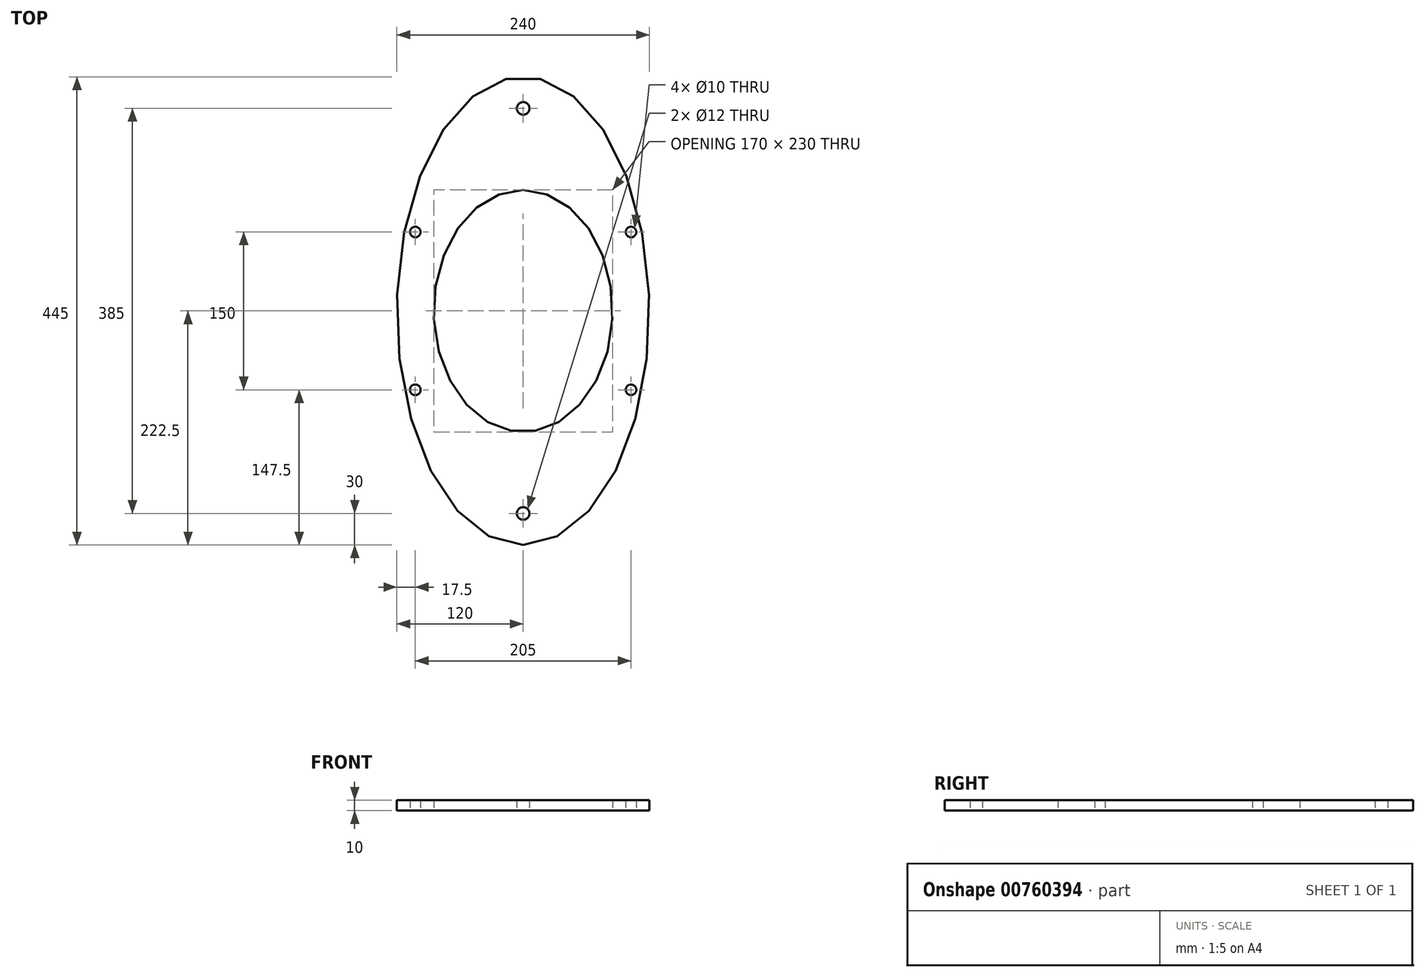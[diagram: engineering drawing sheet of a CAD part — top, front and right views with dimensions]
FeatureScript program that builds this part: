
annotation { "Feature Type Name" : "Feature", "Feature Type Description" : "" }
export const myFeature = defineFeature(function(context is Context, id is Id, definition is map)
    precondition{}
    {
        {
            var Q0;
            Q0=qCreatedBy(makeId("Top.planeOp"),FACE);
            var sketch = newSketch(context, id + "F0", { "sketchPlane" : qUnion([Q0])});
            skPoint(sketch, "E0", {"position": v(150.32, -165.76) * mm});
            skPoint(sketch, "E1", {"position": v(107.37, -221.56) * mm});
            skPoint(sketch, "E2", {"position": v(69.02, -211.72) * mm});
            skPoint(sketch, "E3", {"position": v(0, -246.18) * mm});
            skPoint(sketch, "E4", {"position": v(138.05, -177.25) * mm});
            skPoint(sketch, "E5", {"position": v(146.48, 0) * mm});
            skPoint(sketch, "E6", {"position": v(132.68, -82.88) * mm});
            skLineSegment(sketch, "E7", {"start": v(0, 292) * mm, "end": v(0, -246.18) * mm, "construction": true});
            skPoint(sketch, "E8.MirrorP", {"position": v(-146.48, 0) * mm});
            skPoint(sketch, "E9.MirrorP", {"position": v(-132.68, -82.88) * mm});
            skPoint(sketch, "E10.MirrorP", {"position": v(-150.32, -165.76) * mm});
            skPoint(sketch, "E11.MirrorP", {"position": v(-138.05, -177.25) * mm});
            skPoint(sketch, "E12.MirrorP", {"position": v(-107.37, -221.56) * mm});
            skPoint(sketch, "E13.MirrorP", {"position": v(-69.02, -211.72) * mm});
            skPoint(sketch, "E14", {"position": v(0, 0) * mm});
            skPoint(sketch, "E15", {"position": v(-146.25, -161.4) * mm});
            skPoint(sketch, "E16", {"position": v(-136.87, -189.28) * mm});
            skPoint(sketch, "E17", {"position": v(-146.26, -172.33) * mm});
            skPoint(sketch, "E18", {"position": v(-131.04, -210.06) * mm});
            skPoint(sketch, "E19", {"position": v(-94.82, -218.38) * mm});
            skPoint(sketch, "E20", {"position": v(-60.59, -222.84) * mm});
            skPoint(sketch, "E21", {"position": v(-67.25, -214.49) * mm});
            skPoint(sketch, "E22", {"position": v(-72.48, -210.2) * mm});
            skPoint(sketch, "E23", {"position": v(-119.37, -219.05) * mm});
            skPoint(sketch, "E24", {"position": v(-149.89, -167.68) * mm});
            skPoint(sketch, "E25.MirrorP", {"position": v(60.59, -222.84) * mm});
            skPoint(sketch, "E26.MirrorP", {"position": v(67.25, -214.49) * mm});
            skPoint(sketch, "E27.MirrorP", {"position": v(72.48, -210.2) * mm});
            skPoint(sketch, "E28.MirrorP", {"position": v(94.82, -218.38) * mm});
            skPoint(sketch, "E29.MirrorP", {"position": v(119.37, -219.05) * mm});
            skPoint(sketch, "E30.MirrorP", {"position": v(136.87, -189.28) * mm});
            skPoint(sketch, "E31.MirrorP", {"position": v(146.26, -172.33) * mm});
            skPoint(sketch, "E32.MirrorP", {"position": v(149.89, -167.68) * mm});
            skPoint(sketch, "E33.MirrorP", {"position": v(146.25, -161.4) * mm});
            skPoint(sketch, "E34", {"position": v(-139.73, -175.31) * mm});
            skPoint(sketch, "E35.MirrorP", {"position": v(131.04, -210.06) * mm});
            skPoint(sketch, "E36.MirrorP", {"position": v(-132.68, 82.88) * mm});
            skPoint(sketch, "E37.MirrorP", {"position": v(-139.73, 175.31) * mm});
            skPoint(sketch, "E38.MirrorP", {"position": v(-150.32, 165.76) * mm});
            skPoint(sketch, "E39.MirrorP", {"position": v(69.02, 211.72) * mm});
            skPoint(sketch, "E40.MirrorP", {"position": v(150.32, 165.76) * mm});
            skPoint(sketch, "E41.MirrorP", {"position": v(-67.25, 214.49) * mm});
            skPoint(sketch, "E42.MirrorP", {"position": v(131.04, 210.06) * mm});
            skPoint(sketch, "E43.MirrorP", {"position": v(60.59, 222.84) * mm});
            skPoint(sketch, "E44.MirrorP", {"position": v(119.37, 219.05) * mm});
            skPoint(sketch, "E45.MirrorP", {"position": v(136.87, 189.28) * mm});
            skPoint(sketch, "E46.MirrorP", {"position": v(-72.48, 210.2) * mm});
            skPoint(sketch, "E47.MirrorP", {"position": v(-138.05, 177.25) * mm});
            skPoint(sketch, "E48.MirrorP", {"position": v(-69.02, 211.72) * mm});
            skPoint(sketch, "E49.MirrorP", {"position": v(72.48, 210.2) * mm});
            skPoint(sketch, "E50.MirrorP", {"position": v(-146.25, 161.4) * mm});
            skPoint(sketch, "E51.MirrorP", {"position": v(-136.87, 189.28) * mm});
            skPoint(sketch, "E52.MirrorP", {"position": v(138.05, 177.25) * mm});
            skPoint(sketch, "E53.MirrorP", {"position": v(67.25, 214.49) * mm});
            skPoint(sketch, "E54.MirrorP", {"position": v(-149.89, 167.68) * mm});
            skPoint(sketch, "E55.MirrorP", {"position": v(149.89, 167.68) * mm});
            skPoint(sketch, "E56.MirrorP", {"position": v(-107.37, 221.56) * mm});
            skPoint(sketch, "E57.MirrorP", {"position": v(-94.82, 218.38) * mm});
            skPoint(sketch, "E58.MirrorP", {"position": v(146.26, 172.33) * mm});
            skPoint(sketch, "E59.MirrorP", {"position": v(107.37, 221.56) * mm});
            skPoint(sketch, "E60.MirrorP", {"position": v(-131.04, 210.06) * mm});
            skPoint(sketch, "E61.MirrorP", {"position": v(94.82, 218.38) * mm});
            skPoint(sketch, "E62.MirrorP", {"position": v(146.25, 161.4) * mm});
            skPoint(sketch, "E63.MirrorP", {"position": v(0, 246.18) * mm});
            skPoint(sketch, "E64.MirrorP", {"position": v(-146.26, 172.33) * mm});
            skPoint(sketch, "E65.MirrorP", {"position": v(-119.37, 219.05) * mm});
            skPoint(sketch, "E66.MirrorP", {"position": v(-60.59, 222.84) * mm});
            skPoint(sketch, "E67.MirrorP", {"position": v(132.68, 82.88) * mm});
            skFitSpline(sketch, "E68", {"points": [v(-146.48, 0) * mm, v(-132.68, 82.88) * mm, v(-146.25, 161.4) * mm, v(-150.32, 165.76) * mm, v(-149.89, 167.68) * mm, v(-146.26, 172.33) * mm, v(-139.73, 175.31) * mm, v(-138.05, 177.25) * mm, v(-136.87, 189.28) * mm, v(-131.04, 210.06) * mm, v(-119.37, 219.05) * mm, v(-107.37, 221.56) * mm, v(-94.82, 218.38) * mm, v(-72.48, 210.2) * mm, v(-69.02, 211.72) * mm, v(-67.25, 214.49) * mm, v(-60.59, 222.84) * mm, v(0, 246.18) * mm, v(60.59, 222.84) * mm, v(67.25, 214.49) * mm, v(69.02, 211.72) * mm, v(72.48, 210.2) * mm, v(94.82, 218.38) * mm, v(107.37, 221.56) * mm, v(119.37, 219.05) * mm, v(131.04, 210.06) * mm, v(136.87, 189.28) * mm, v(138.05, 177.25) * mm, v(146.26, 172.33) * mm, v(149.89, 167.68) * mm, v(150.32, 165.76) * mm, v(146.25, 161.4) * mm, v(132.68, 82.88) * mm, v(146.48, 0) * mm, v(132.68, -82.88) * mm, v(146.25, -161.4) * mm, v(150.32, -165.76) * mm, v(149.89, -167.68) * mm, v(146.26, -172.33) * mm, v(138.05, -177.25) * mm, v(136.87, -189.28) * mm, v(131.04, -210.06) * mm, v(119.37, -219.05) * mm, v(107.37, -221.56) * mm, v(94.82, -218.38) * mm, v(72.48, -210.2) * mm, v(69.02, -211.72) * mm, v(67.25, -214.49) * mm, v(60.59, -222.84) * mm, v(0, -246.18) * mm, v(-60.59, -222.84) * mm, v(-67.25, -214.49) * mm, v(-69.02, -211.72) * mm, v(-72.48, -210.2) * mm, v(-94.82, -218.38) * mm, v(-107.37, -221.56) * mm, v(-119.37, -219.05) * mm, v(-131.04, -210.06) * mm, v(-136.87, -189.28) * mm, v(-138.05, -177.25) * mm, v(-139.73, -175.31) * mm, v(-146.26, -172.33) * mm, v(-149.89, -167.68) * mm, v(-150.32, -165.76) * mm, v(-146.25, -161.4) * mm, v(-132.68, -82.88) * mm, v(-146.48, 0) * mm]});
            skPoint(sketch, "E69", {"position": v(0, 295) * mm});
            skPoint(sketch, "E70", {"position": v(-30, 295) * mm});
            skPoint(sketch, "E71", {"position": v(-225, 0) * mm});
            skPoint(sketch, "E72", {"position": v(-225, 100) * mm});
            skPoint(sketch, "E73.MirrorP", {"position": v(225, 100) * mm});
            skPoint(sketch, "E74.MirrorP", {"position": v(225, -60) * mm});
            skPoint(sketch, "E75.2.0", {"position": v(-17.6, -30.48) * mm});
            skPoint(sketch, "E75.center", {"position": v(-17.6, -10.16) * mm});
            skLineSegment(sketch, "E76", {"start": v(-225, 0) * mm, "end": v(-225, 100) * mm});
            skLineSegment(sketch, "E77", {"start": v(-30, 295) * mm, "end": v(0, 295) * mm});
            skPoint(sketch, "E78", {"position": v(-30, 100) * mm});
            skArc(sketch, "E79", {"start": v(-30, 295) * mm, "mid": v(-167.89, 237.89) * mm, "end": v(-225, 100) * mm});
            skLineSegment(sketch, "E80.MirrorCS", {"start": v(225, 0) * mm, "end": v(225, 100) * mm});
            skArc(sketch, "E81.MirrorCS", {"start": v(30, 295) * mm, "mid": v(167.89, 237.89) * mm, "end": v(225, 100) * mm});
            skLineSegment(sketch, "E82.MirrorCS", {"start": v(30, 295) * mm, "end": v(0, 295) * mm});
            skArc(sketch, "E83.MirrorCS", {"start": v(-30, -295) * mm, "mid": v(-167.89, -237.89) * mm, "end": v(-225, -100) * mm});
            skLineSegment(sketch, "E84.MirrorCS", {"start": v(-225, 0) * mm, "end": v(-225, -100) * mm});
            skLineSegment(sketch, "E85.MirrorCS", {"start": v(225, 0) * mm, "end": v(225, -100) * mm});
            skArc(sketch, "E86.MirrorCS", {"start": v(30, -295) * mm, "mid": v(167.89, -237.89) * mm, "end": v(225, -100) * mm});
            skLineSegment(sketch, "E87.MirrorCS", {"start": v(30, -295) * mm, "end": v(0, -295) * mm});
            skLineSegment(sketch, "E88.MirrorCS", {"start": v(-30, -295) * mm, "end": v(0, -295) * mm});
            skEllipse(sketch, "E89", {"center": v(0, 0) * mm, "majorRadius": 120 * mm, "minorRadius": 222.5 * mm, "majorAxis": v(-1, 0)});
            skEllipse(sketch, "E90", {"center": v(0, 0) * mm, "majorRadius": 115 * mm, "minorRadius": 85 * mm, "majorAxis": v(0, 1)});
            skPoint(sketch, "E91", {"position": v(-102.5, 75) * mm});
            skCircle(sketch, "E92", {"center": v(-102.5, 75) * mm, "radius": 5 * mm});
            skCircle(sketch, "E93.MirrorC", {"center": v(102.5, 75) * mm, "radius": 5 * mm});
            skCircle(sketch, "E94.MirrorC", {"center": v(-102.5, -75) * mm, "radius": 5 * mm});
            skCircle(sketch, "E95.MirrorC", {"center": v(102.5, -75) * mm, "radius": 5 * mm});
            skCircle(sketch, "E96", {"center": v(0, 192.5) * mm, "radius": 6 * mm});
            skCircle(sketch, "E97.MirrorC", {"center": v(0, -192.5) * mm, "radius": 6 * mm});
            skSolve(sketch);
        }
        {
            var Q0;
            Q0=makeQuery(id+"F0.imprint","IMPRINT",FACE,{"disambiguationData":[TD([[makeQuery(id+"F0.imprint","IMPRINT",EDGE,{"derivedFrom":sQuery(id+"F0.wireOp",EDGE,"E89")}),1.0]])]});
            extrude(context, id + "F1", {"entities" : qUnion([Q0]), "depth" : 10 * mm, "offsetDistance" : 25 * mm});
        }
        {
            var Q0;
            Q0=makeQuery(id+"F1.opExtrude","CAP_FACE",FACE,{"disambiguationData":[OSD([sQuery(id+"F0.wireOp",EDGE,"E89"),sQuery(id+"F0.wireOp",EDGE,"E90"),sQuery(id+"F0.wireOp",EDGE,"E92"),sQuery(id+"F0.wireOp",EDGE,"E93.MirrorC"),sQuery(id+"F0.wireOp",EDGE,"E94.MirrorC"),sQuery(id+"F0.wireOp",EDGE,"E95.MirrorC"),sQuery(id+"F0.wireOp",EDGE,"E96"),sQuery(id+"F0.wireOp",EDGE,"E97.MirrorC")])],"isStart":false});
            cPlane(context, id + "F2", {"entities" : qUnion([Q0]), "cplaneType" : CPlaneType.OFFSET, "offset" : 50 * mm, "width" : 150 * mm, "height" : 150 * mm});
        }
    });
